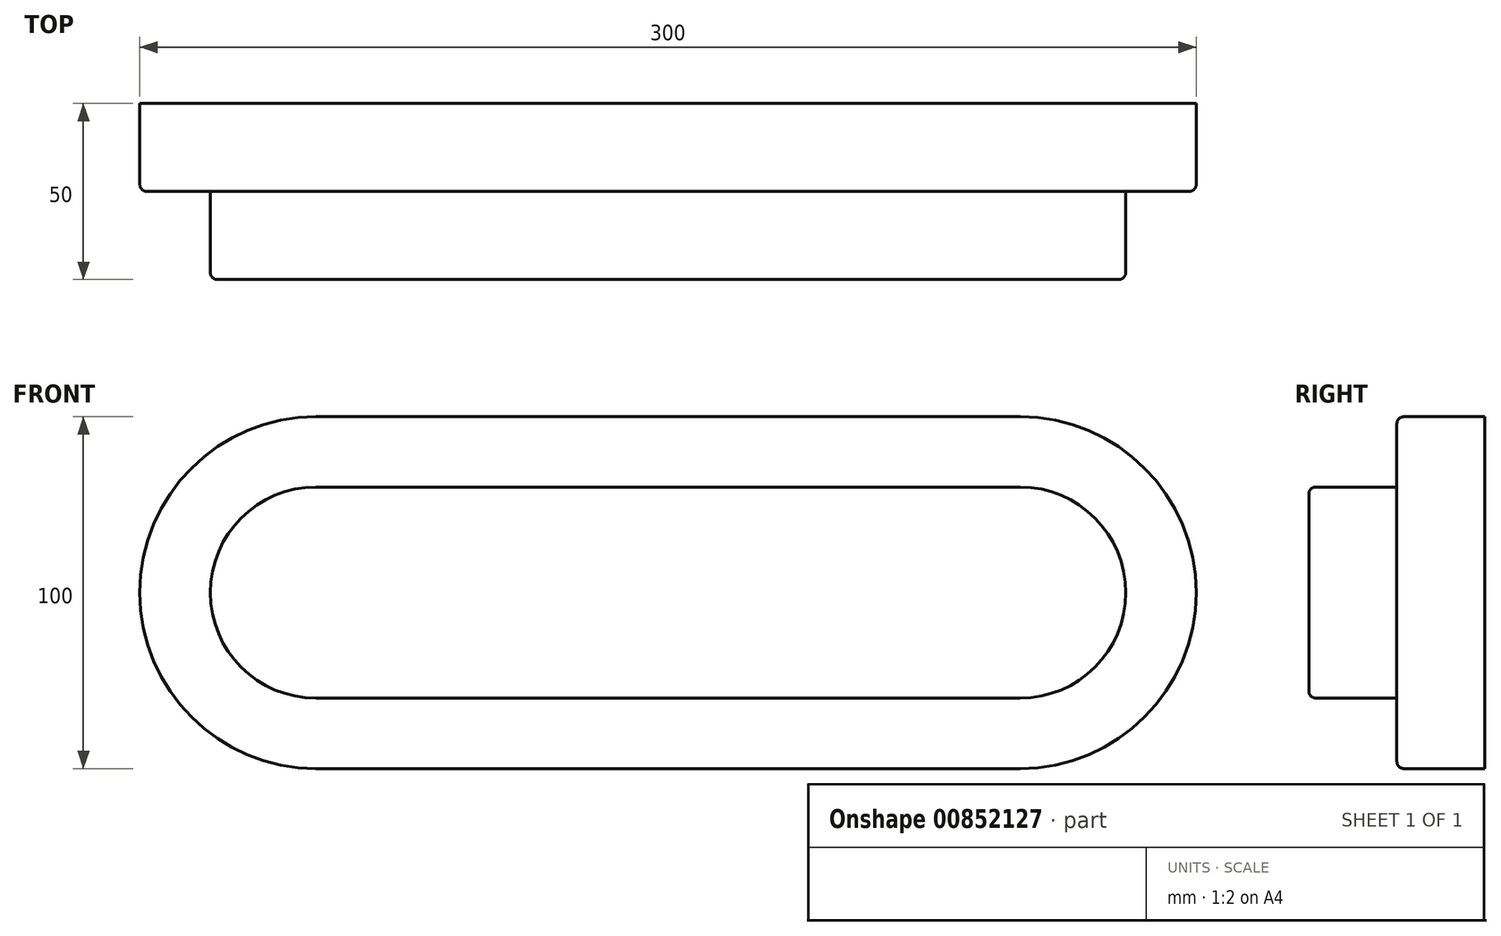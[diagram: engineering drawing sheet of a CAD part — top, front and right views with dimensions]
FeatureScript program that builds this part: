
annotation { "Feature Type Name" : "Feature", "Feature Type Description" : "" }
export const myFeature = defineFeature(function(context is Context, id is Id, definition is map)
    precondition{}
    {
        {
            var Q0;
            Q0=qCreatedBy(makeId("Front.planeOp"),FACE);
            var sketch = newSketch(context, id + "F0", { "sketchPlane" : qUnion([Q0])});
            skLineSegment(sketch, "E0.bottom", {"start": v(100, -50) * mm, "end": v(-100, -50) * mm});
            skLineSegment(sketch, "E0.top", {"start": v(100, 50) * mm, "end": v(-100, 50) * mm});
            skLineSegment(sketch, "E0.left", {"start": v(150, 0) * mm, "end": v(150, 0) * mm});
            skLineSegment(sketch, "E0.right", {"start": v(-150, 0) * mm, "end": v(-150, 0) * mm});
            skPoint(sketch, "E0.middle", {"position": v(0, 0) * mm});
            skPoint(sketch, "E1.visualSharp", {"position": v(-150, 50) * mm});
            skArc(sketch, "E1.filletArc", {"start": v(-100, 50) * mm, "mid": v(-135.36, 35.36) * mm, "end": v(-150, 0) * mm});
            skPoint(sketch, "E2.visualSharp", {"position": v(-150, -50) * mm});
            skArc(sketch, "E2.filletArc", {"start": v(-150, 0) * mm, "mid": v(-135.36, -35.36) * mm, "end": v(-100, -50) * mm});
            skPoint(sketch, "E3.visualSharp", {"position": v(150, 50) * mm});
            skArc(sketch, "E3.filletArc", {"start": v(150, 0) * mm, "mid": v(135.36, 35.36) * mm, "end": v(100, 50) * mm});
            skPoint(sketch, "E4.visualSharp", {"position": v(150, -50) * mm});
            skArc(sketch, "E4.filletArc", {"start": v(100, -50) * mm, "mid": v(135.36, -35.36) * mm, "end": v(150, 0) * mm});
            skLineSegment(sketch, "E5.bottom", {"start": v(100, -30) * mm, "end": v(-100, -30) * mm});
            skLineSegment(sketch, "E5.top", {"start": v(100, 30) * mm, "end": v(-100, 30) * mm});
            skLineSegment(sketch, "E5.left", {"start": v(130, 0) * mm, "end": v(130, 0) * mm});
            skLineSegment(sketch, "E5.right", {"start": v(-130, 0) * mm, "end": v(-130, 0) * mm});
            skPoint(sketch, "E6.visualSharp", {"position": v(130, 30) * mm});
            skArc(sketch, "E6.filletArc", {"start": v(130, 0) * mm, "mid": v(121.21, 21.21) * mm, "end": v(100, 30) * mm});
            skPoint(sketch, "E7.visualSharp", {"position": v(-130, 30) * mm});
            skArc(sketch, "E7.filletArc", {"start": v(-100, 30) * mm, "mid": v(-121.21, 21.21) * mm, "end": v(-130, 0) * mm});
            skPoint(sketch, "E8.visualSharp", {"position": v(-130, -30) * mm});
            skArc(sketch, "E8.filletArc", {"start": v(-130, 0) * mm, "mid": v(-121.21, -21.21) * mm, "end": v(-100, -30) * mm});
            skPoint(sketch, "E9.visualSharp", {"position": v(130, -30) * mm});
            skArc(sketch, "E9.filletArc", {"start": v(100, -30) * mm, "mid": v(121.21, -21.21) * mm, "end": v(130, 0) * mm});
            skSolve(sketch);
        }
        {
            var Q0;
            Q0=makeQuery(id+"F0.imprint","IMPRINT",FACE,{"disambiguationData":[TD([[makeQuery(id+"F0.imprint","IMPRINT",EDGE,{"derivedFrom":sQuery(id+"F0.wireOp",EDGE,"E5.bottom")}),-1.0]])]});
            extrude(context, id + "F1", {"entities" : qUnion([Q0]), "depth" : 50 * mm, "offsetDistance" : 25 * mm});
        }
        {
            var Q0;
            Q0=makeQuery(id+"F0.imprint","IMPRINT",FACE,{"disambiguationData":[TD([[makeQuery(id+"F0.imprint","IMPRINT",EDGE,{"derivedFrom":sQuery(id+"F0.wireOp",EDGE,"E0.bottom")}),-1.0]])]});
            extrude(context, id + "F2", {"entities" : qUnion([Q0]), "operationType" : NewBodyOperationType.ADD, "depth" : 25 * mm, "offsetDistance" : 25 * mm});
        }
        {
            var Q0;
            Q0=makeQuery(id+"F2.opExtrude","CAP_EDGE",EDGE,{"disambiguationData":[OSD([sQuery(id+"F0.wireOp",EDGE,"E1.filletArc"),sQuery(id+"F0.wireOp",EDGE,"E2.filletArc")])],"isStart":false});
            var Q1;
            Q1=makeQuery(id+"F1.opExtrude","CAP_EDGE",EDGE,{"disambiguationData":[OSD([sQuery(id+"F0.wireOp",EDGE,"E5.bottom")])],"isStart":false});
            fillet(context, id + "F3", {"entities" : qUnion([Q0, Q1]), "radius" : 2 * mm, "tangentPropagation" : true, "allowEdgeOverflow" : false});
        }
    });
